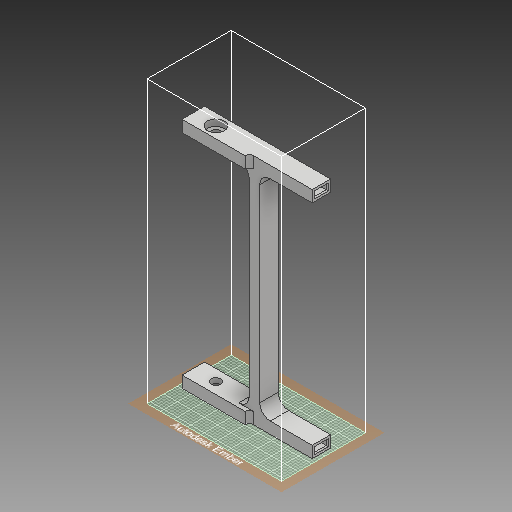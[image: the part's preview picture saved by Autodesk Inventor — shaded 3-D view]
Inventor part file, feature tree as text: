
AUTODESK INVENTOR PART (.ipt)
format: ipt  version: 2018 (Build 220112000, 112)  size: 389,632 bytes
history: native  units: mm
features: sketch x10, extrude x9, fillet x4
ambient origin geometry x8: Origin, YZ Plane, XZ Plane, XY Plane, X Axis, Y Axis, Z Axis, Center Point
bodies: Solid1 (feature_tree)
feature tree (23):
  extrude  "Extrusion1"  Depth=5.5118mm
  extrude  "Extrusion2"  Depth=2.3368mm
  extrude  "Extrusion3"  Depth=5.5118mm
  fillet  "Fillet1"  Radius=5.588mm
  fillet  "Fillet2"  Radius=2.3368mm
  extrude  "Extrusion4"  Depth=5.0mm
  extrude  "Extrusion5"  Depth=10.763mm
  extrude  "Extrusion6"  Depth=30.0mm TaperAngle=0.0deg
  extrude  "Extrusion7"  Depth=5.0mm
  fillet  "Fillet3"  Radius=10.763mm
  sketch  "Sketch8"  dims[d22=8.1mm d23=114.75mm d24=0.0mm]
  extrude  "Extrusion8"  Depth=114.75mm TaperAngle=0.0deg
  extrude  "Extrusion9"  Depth=2.412mm TaperAngle=0.0deg
  fillet  "Fillet4"  Radius=4.5mm
  sketch  "Sketch1"  dims[d0=8.763mm d1=5.5118mm]
  sketch  "Sketch2"  dims[d4=5.588mm d5=2.3368mm]
  sketch  "Sketch3"  dims[d6=8.763mm d7=5.5118mm d8=5.588mm d9=2.3368mm]
  sketch  "Sketch4"  dims[d10=30.0mm d11=0.0mm d12=5.0mm]
  sketch  "Sketch5"  dims[d13=111.0mm d14=0.0mm d15=10.763mm]
  sketch  "Sketch6"  dims[d16=10.763mm d17=30.0mm d18=0.0mm]
  sketch  "Sketch7"  dims[d19=2.0mm d20=5.0mm d21=10.763mm]
  sketch  "Sketch9"  dims[d25=2.412mm d26=0.0mm d27=2.412mm d28=0.0mm d29=4.5mm]
  sketch  "Sketch10"  dims[d30=115.0mm d31=0.0mm d32=0.5mm d33=8.763mm d34=8.763mm d35=29.5mm d36=0.0mm d37=6.5mm d38=6.5mm d39=24.75mm d40=0.0mm d41=3.25mm]
